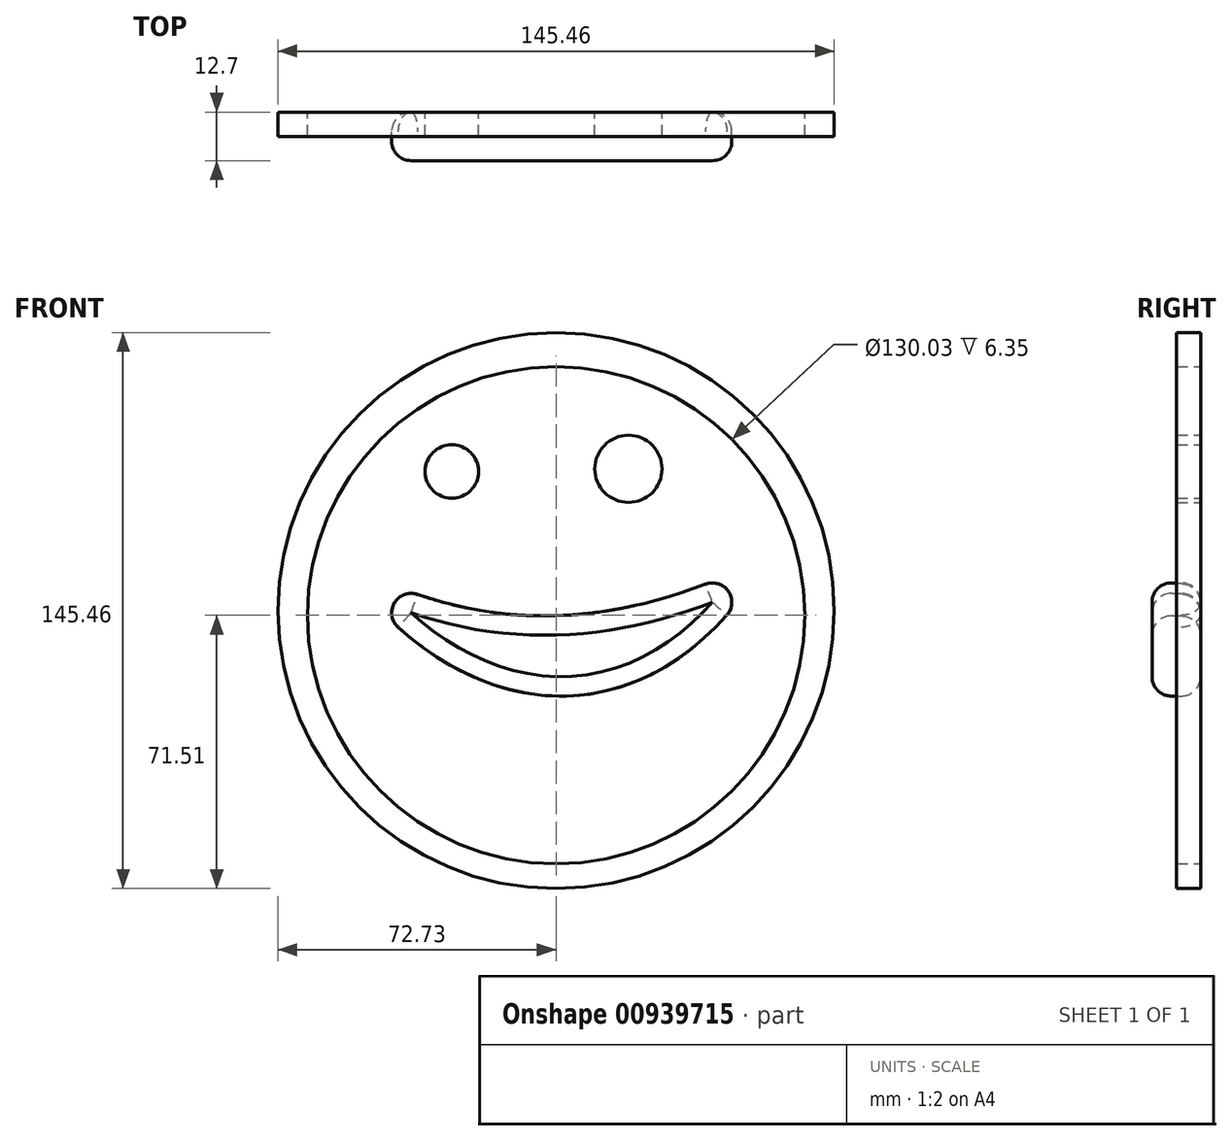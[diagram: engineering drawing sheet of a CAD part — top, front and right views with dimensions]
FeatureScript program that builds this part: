
annotation { "Feature Type Name" : "Feature", "Feature Type Description" : "" }
export const myFeature = defineFeature(function(context is Context, id is Id, definition is map)
    precondition{}
    {
        {
            var Q0;
            Q0=qCreatedBy(makeId("Front.planeOp"),FACE);
            var sketch = newSketch(context, id + "F0", { "sketchPlane" : qUnion([Q0])});
            skFitSpline(sketch, "E0", {"points": [v(-56.86, 14.68) * mm, v(55.94, 15.61) * mm], "startDerivative": vector(95.6, -137.46) * mm, "endDerivative": vector(90.01, 152.8) * mm});
            skFitSpline(sketch, "E1", {"points": [v(-56.86, 14.68) * mm, v(55.94, 15.61) * mm], "startDerivative": vector(114.43, -63.5) * mm, "endDerivative": vector(116.53, 58.61) * mm});
            skCircle(sketch, "E2", {"center": v(0, 0) * mm, "radius": 65.01 * mm});
            skCircle(sketch, "E3", {"center": v(0, 1.22) * mm, "radius": 72.73 * mm});
            skCircle(sketch, "E4", {"center": v(-27.27, 37.62) * mm, "radius": 7 * mm});
            skCircle(sketch, "E5", {"center": v(18.9, 38.32) * mm, "radius": 8.8 * mm});
            skSolve(sketch);
        }
        {
            var Q0;
            Q0=makeQuery(id+"F0.imprint","IMPRINT",FACE,{"disambiguationData":[TD([[makeQuery(id+"F0.imprint","IMPRINT",EDGE,{"derivedFrom":sQuery(id+"F0.wireOp",EDGE,"E0")}),1.0]])]});
            extrude(context, id + "F1", {"entities" : qUnion([Q0]), "depth" : 12.7 * mm, "offsetDistance" : 25.4 * mm});
        }
        {
            var Q0;
            {var subQ0=sQuery(id+"F0.wireOp",EDGE,"E1");var subQ1=sQuery(id+"F0.wireOp",EDGE,"E0");Q0=makeQuery(id+"F1.opExtrude","SWEPT_EDGE",EDGE,{"disambiguationData":[OSD([subQ1,subQ0]),TDD([makeQuery(id+"F0.imprint","INTERSECT",VERTEX,{"disambiguationData":[OD(0.0)],"derivedFrom":[subQ1,subQ0]})])]});}
            var Q1;
            Q1=makeQuery(id+"F1.opExtrude","CAP_EDGE",EDGE,{"disambiguationData":[OSD([sQuery(id+"F0.wireOp",EDGE,"E0")])],"isStart":false});
            var Q2;
            Q2=makeQuery(id+"F1.opExtrude","SWEPT_FACE",FACE,{"disambiguationData":[OSD([sQuery(id+"F0.wireOp",EDGE,"E1")])]});
            fillet(context, id + "F2", {"entities" : qUnion([Q0, Q1, Q2]), "radius" : 5.08 * mm, "tangentPropagation" : true, "allowEdgeOverflow" : false});
        }
        {
            var Q0;
            Q0=makeQuery(id+"F1.opExtrude","CAP_EDGE",EDGE,{"disambiguationData":[OSD([sQuery(id+"F0.wireOp",EDGE,"E0")])],"isStart":true});
            fillet(context, id + "F3", {"entities" : qUnion([Q0]), "radius" : 5.08 * mm, "tangentPropagation" : true, "allowEdgeOverflow" : false});
        }
        {
            var Q0;
            Q0=makeQuery(id+"F0.imprint","IMPRINT",FACE,{"disambiguationData":[TD([[makeQuery(id+"F0.imprint","IMPRINT",EDGE,{"derivedFrom":sQuery(id+"F0.wireOp",EDGE,"E2")}),-1.0]])]});
            extrude(context, id + "F4", {"entities" : qUnion([Q0]), "depth" : 6.35 * mm, "offsetDistance" : 25.4 * mm});
        }
        {
            var Q0;
            Q0=makeQuery(id+"F0.imprint","IMPRINT",FACE,{"disambiguationData":[TD([[makeQuery(id+"F0.imprint","IMPRINT",EDGE,{"derivedFrom":sQuery(id+"F0.wireOp",EDGE,"E4")}),1.0]])]});
            var Q1;
            Q1=makeQuery(id+"F0.imprint","IMPRINT",FACE,{"disambiguationData":[TD([[makeQuery(id+"F0.imprint","IMPRINT",EDGE,{"derivedFrom":sQuery(id+"F0.wireOp",EDGE,"E5")}),1.0]])]});
            extrude(context, id + "F5", {"entities" : qUnion([Q0, Q1]), "depth" : 6.35 * mm, "offsetDistance" : 25.4 * mm});
        }
    });
